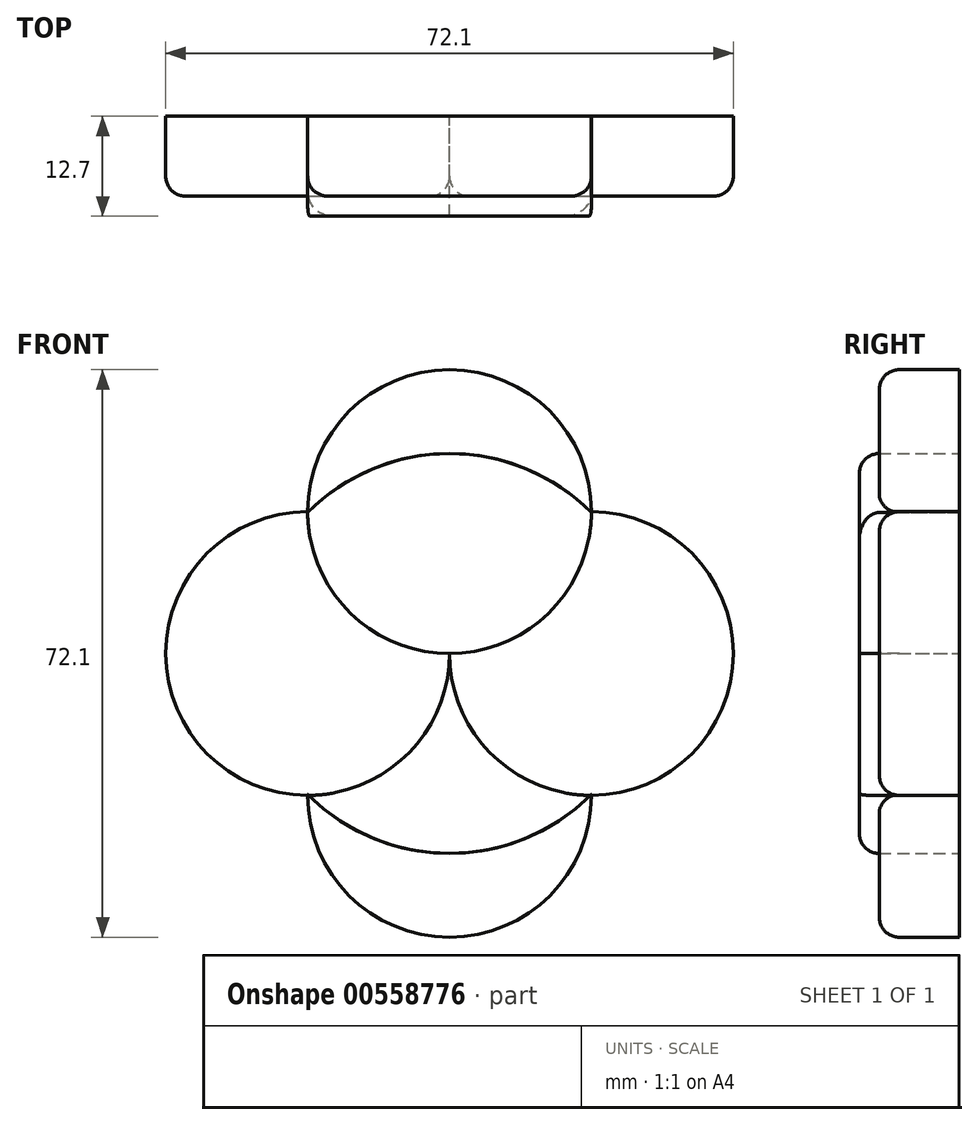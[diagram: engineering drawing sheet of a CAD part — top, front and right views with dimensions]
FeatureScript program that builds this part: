
annotation { "Feature Type Name" : "Feature", "Feature Type Description" : "" }
export const myFeature = defineFeature(function(context is Context, id is Id, definition is map)
    precondition{}
    {
        {
            var Q0;
            Q0=qCreatedBy(makeId("Front.planeOp"),FACE);
            var sketch = newSketch(context, id + "F0", { "sketchPlane" : qUnion([Q0])});
            skCircle(sketch, "E0", {"center": v(0, 18.02) * mm, "radius": 18.02 * mm});
            skCircle(sketch, "E1", {"center": v(18.02, 0) * mm, "radius": 18.02 * mm});
            skCircle(sketch, "E2", {"center": v(0, -18.02) * mm, "radius": 18.02 * mm});
            skCircle(sketch, "E3", {"center": v(-18.02, 0) * mm, "radius": 18.02 * mm});
            skCircle(sketch, "E4", {"center": v(0, 0) * mm, "radius": 25.4 * mm});
            skSolve(sketch);
        }
        {
            var Q0;
            {var subQ0=sQuery(id+"F0.wireOp",EDGE,"E4");var subQ1=sQuery(id+"F0.wireOp",EDGE,"E1");var subQ2=makeQuery(id+"F0.imprint","INTERSECT",VERTEX,{"disambiguationData":[OD(0.0)],"derivedFrom":[subQ1,subQ0]});Q0=makeQuery(id+"F0.imprint","IMPRINT",FACE,{"disambiguationData":[TD([[makeQuery(id+"F0.imprint","IMPRINT",EDGE,{"disambiguationData":[TD([[subQ2,-1.0]])],"derivedFrom":subQ0}),1.0]])]});}
            var Q1;
            {var subQ0=sQuery(id+"F0.wireOp",EDGE,"E4");var subQ1=sQuery(id+"F0.wireOp",EDGE,"E0");var subQ2=makeQuery(id+"F0.imprint","INTERSECT",VERTEX,{"disambiguationData":[OD(0.0)],"derivedFrom":[subQ1,subQ0]});Q1=makeQuery(id+"F0.imprint","IMPRINT",FACE,{"disambiguationData":[TD([[makeQuery(id+"F0.imprint","IMPRINT",EDGE,{"disambiguationData":[TD([[subQ2,-1.0]])],"derivedFrom":subQ0}),1.0]])]});}
            var Q2;
            {var subQ0=sQuery(id+"F0.wireOp",EDGE,"E4");var subQ1=sQuery(id+"F0.wireOp",EDGE,"E0");var subQ2=makeQuery(id+"F0.imprint","INTERSECT",VERTEX,{"disambiguationData":[OD(1.0)],"derivedFrom":[subQ1,subQ0]});Q2=makeQuery(id+"F0.imprint","IMPRINT",FACE,{"disambiguationData":[TD([[makeQuery(id+"F0.imprint","IMPRINT",EDGE,{"disambiguationData":[TD([[subQ2,1.0]])],"derivedFrom":subQ0}),1.0]])]});}
            var Q3;
            {var subQ0=sQuery(id+"F0.wireOp",EDGE,"E4");var subQ1=sQuery(id+"F0.wireOp",EDGE,"E1");var subQ2=makeQuery(id+"F0.imprint","INTERSECT",VERTEX,{"disambiguationData":[OD(1.0)],"derivedFrom":[subQ1,subQ0]});Q3=makeQuery(id+"F0.imprint","IMPRINT",FACE,{"disambiguationData":[TD([[makeQuery(id+"F0.imprint","IMPRINT",EDGE,{"disambiguationData":[TD([[subQ2,1.0]])],"derivedFrom":subQ0}),1.0]])]});}
            extrude(context, id + "F1", {"entities" : qUnion([Q0, Q1, Q2, Q3]), "depth" : 12.7 * mm, "offsetDistance" : 25.4 * mm});
        }
        {
            var Q0;
            {var subQ0=sQuery(id+"F0.wireOp",EDGE,"E4");var subQ1=sQuery(id+"F0.wireOp",EDGE,"E0");var subQ2=makeQuery(id+"F0.imprint","INTERSECT",VERTEX,{"disambiguationData":[OD(0.0)],"derivedFrom":[subQ1,subQ0]});Q0=makeQuery(id+"F0.imprint","IMPRINT",FACE,{"disambiguationData":[TD([[makeQuery(id+"F0.imprint","IMPRINT",EDGE,{"disambiguationData":[TD([[subQ2,1.0]])],"derivedFrom":subQ0}),1.0]])]});}
            var Q1;
            {var subQ0=sQuery(id+"F0.wireOp",EDGE,"E4");var subQ1=sQuery(id+"F0.wireOp",EDGE,"E0");var subQ2=makeQuery(id+"F0.imprint","INTERSECT",VERTEX,{"disambiguationData":[OD(1.0)],"derivedFrom":[subQ1,subQ0]});Q1=makeQuery(id+"F0.imprint","IMPRINT",FACE,{"disambiguationData":[TD([[makeQuery(id+"F0.imprint","IMPRINT",EDGE,{"disambiguationData":[TD([[subQ2,-1.0]])],"derivedFrom":subQ0}),1.0]])]});}
            var Q2;
            {var subQ0=sQuery(id+"F0.wireOp",EDGE,"E4");var subQ1=sQuery(id+"F0.wireOp",EDGE,"E2");var subQ2=makeQuery(id+"F0.imprint","INTERSECT",VERTEX,{"disambiguationData":[OD(1.0)],"derivedFrom":[subQ1,subQ0]});Q2=makeQuery(id+"F0.imprint","IMPRINT",FACE,{"disambiguationData":[TD([[makeQuery(id+"F0.imprint","IMPRINT",EDGE,{"disambiguationData":[TD([[subQ2,-1.0]])],"derivedFrom":subQ0}),1.0]])]});}
            var Q3;
            {var subQ0=sQuery(id+"F0.wireOp",EDGE,"E4");var subQ1=sQuery(id+"F0.wireOp",EDGE,"E1");var subQ2=makeQuery(id+"F0.imprint","INTERSECT",VERTEX,{"disambiguationData":[OD(1.0)],"derivedFrom":[subQ1,subQ0]});Q3=makeQuery(id+"F0.imprint","IMPRINT",FACE,{"disambiguationData":[TD([[makeQuery(id+"F0.imprint","IMPRINT",EDGE,{"disambiguationData":[TD([[subQ2,-1.0]])],"derivedFrom":subQ0}),1.0]])]});}
            var Q4;
            {var subQ0=sQuery(id+"F0.wireOp",EDGE,"E3");var subQ1=sQuery(id+"F0.wireOp",EDGE,"E0");var subQ2=makeQuery(id+"F0.imprint","INTERSECT",VERTEX,{"derivedFrom":[subQ1,subQ0]});Q4=makeQuery(id+"F0.imprint","IMPRINT",FACE,{"disambiguationData":[TD([[makeQuery(id+"F0.imprint","IMPRINT",EDGE,{"disambiguationData":[TD([[subQ2,1.0]])],"derivedFrom":subQ1}),1.0]])]});}
            var Q5;
            {var subQ0=sQuery(id+"F0.wireOp",EDGE,"E1");var subQ1=sQuery(id+"F0.wireOp",EDGE,"E0");var subQ2=makeQuery(id+"F0.imprint","INTERSECT",VERTEX,{"derivedFrom":[subQ1,subQ0]});Q5=makeQuery(id+"F0.imprint","IMPRINT",FACE,{"disambiguationData":[TD([[makeQuery(id+"F0.imprint","IMPRINT",EDGE,{"disambiguationData":[TD([[subQ2,1.0]])],"derivedFrom":subQ1}),-1.0]])]});}
            var Q6;
            {var subQ0=sQuery(id+"F0.wireOp",EDGE,"E3");var subQ1=sQuery(id+"F0.wireOp",EDGE,"E0");var subQ2=makeQuery(id+"F0.imprint","INTERSECT",VERTEX,{"derivedFrom":[subQ1,subQ0]});Q6=makeQuery(id+"F0.imprint","IMPRINT",FACE,{"disambiguationData":[TD([[makeQuery(id+"F0.imprint","IMPRINT",EDGE,{"disambiguationData":[TD([[subQ2,-1.0]])],"derivedFrom":subQ1}),-1.0]])]});}
            var Q7;
            {var subQ0=sQuery(id+"F0.wireOp",EDGE,"E2");var subQ1=sQuery(id+"F0.wireOp",EDGE,"E1");var subQ2=makeQuery(id+"F0.imprint","INTERSECT",VERTEX,{"derivedFrom":[subQ1,subQ0]});Q7=makeQuery(id+"F0.imprint","IMPRINT",FACE,{"disambiguationData":[TD([[makeQuery(id+"F0.imprint","IMPRINT",EDGE,{"disambiguationData":[TD([[subQ2,1.0]])],"derivedFrom":subQ1}),-1.0]])]});}
            extrude(context, id + "F2", {"entities" : qUnion([Q0, Q1, Q2, Q3, Q4, Q5, Q6, Q7]), "depth" : 10.16 * mm, "offsetDistance" : 25.4 * mm});
        }
        {
            var Q0;
            {var subQ0=sQuery(id+"F0.wireOp",EDGE,"E2");Q0=makeQuery(id+"F2.opExtrude","CAP_EDGE",EDGE,{"disambiguationData":[OSD([subQ0]),TDD([makeQuery(id+"F0.imprint","IMPRINT",EDGE,{"disambiguationData":[TD([[makeQuery(id+"F0.imprint","INTERSECT",VERTEX,{"derivedFrom":[sQuery(id+"F0.wireOp",EDGE,"E1"),subQ0]}),1.0]])],"derivedFrom":subQ0})])],"isStart":false});}
            var Q1;
            {var subQ0=sQuery(id+"F0.wireOp",EDGE,"E1");Q1=makeQuery(id+"F2.opExtrude","CAP_EDGE",EDGE,{"disambiguationData":[OSD([subQ0]),TDD([makeQuery(id+"F0.imprint","IMPRINT",EDGE,{"disambiguationData":[TD([[makeQuery(id+"F0.imprint","INTERSECT",VERTEX,{"derivedFrom":[sQuery(id+"F0.wireOp",EDGE,"E0"),subQ0]}),1.0]])],"derivedFrom":subQ0})])],"isStart":false});}
            var Q2;
            {var subQ0=sQuery(id+"F0.wireOp",EDGE,"E0");Q2=makeQuery(id+"F2.opExtrude","CAP_EDGE",EDGE,{"disambiguationData":[OSD([subQ0]),TDD([makeQuery(id+"F0.imprint","IMPRINT",EDGE,{"disambiguationData":[TD([[makeQuery(id+"F0.imprint","INTERSECT",VERTEX,{"derivedFrom":[subQ0,sQuery(id+"F0.wireOp",EDGE,"E3")]}),1.0]])],"derivedFrom":subQ0})])],"isStart":false});}
            var Q3;
            {var subQ0=sQuery(id+"F0.wireOp",EDGE,"E3");Q3=makeQuery(id+"F2.opExtrude","CAP_EDGE",EDGE,{"disambiguationData":[OSD([subQ0]),TDD([makeQuery(id+"F0.imprint","IMPRINT",EDGE,{"disambiguationData":[TD([[makeQuery(id+"F0.imprint","INTERSECT",VERTEX,{"derivedFrom":[sQuery(id+"F0.wireOp",EDGE,"E0"),subQ0]}),-1.0]])],"derivedFrom":subQ0})])],"isStart":false});}
            var Q4;
            {var subQ0=sQuery(id+"F0.wireOp",EDGE,"E4");Q4=makeQuery(id+"F1.opExtrude","CAP_EDGE",EDGE,{"disambiguationData":[OSD([subQ0]),TDD([makeQuery(id+"F0.imprint","IMPRINT",EDGE,{"disambiguationData":[TD([[makeQuery(id+"F0.imprint","INTERSECT",VERTEX,{"disambiguationData":[OD(1.0)],"derivedFrom":[sQuery(id+"F0.wireOp",EDGE,"E0"),subQ0]}),1.0]])],"derivedFrom":subQ0})])],"isStart":false});}
            var Q5;
            {var subQ0=sQuery(id+"F0.wireOp",EDGE,"E4");Q5=makeQuery(id+"F1.opExtrude","CAP_EDGE",EDGE,{"disambiguationData":[OSD([subQ0]),TDD([makeQuery(id+"F0.imprint","IMPRINT",EDGE,{"disambiguationData":[TD([[makeQuery(id+"F0.imprint","INTERSECT",VERTEX,{"disambiguationData":[OD(0.0)],"derivedFrom":[sQuery(id+"F0.wireOp",EDGE,"E1"),subQ0]}),-1.0]])],"derivedFrom":subQ0})])],"isStart":false});}
            var Q6;
            {var subQ0=sQuery(id+"F0.wireOp",EDGE,"E4");Q6=makeQuery(id+"F1.opExtrude","CAP_EDGE",EDGE,{"disambiguationData":[OSD([subQ0]),TDD([makeQuery(id+"F0.imprint","IMPRINT",EDGE,{"disambiguationData":[TD([[makeQuery(id+"F0.imprint","INTERSECT",VERTEX,{"disambiguationData":[OD(0.0)],"derivedFrom":[sQuery(id+"F0.wireOp",EDGE,"E0"),subQ0]}),-1.0]])],"derivedFrom":subQ0})])],"isStart":false});}
            var Q7;
            {var subQ0=sQuery(id+"F0.wireOp",EDGE,"E4");Q7=makeQuery(id+"F1.opExtrude","CAP_EDGE",EDGE,{"disambiguationData":[OSD([subQ0]),TDD([makeQuery(id+"F0.imprint","IMPRINT",EDGE,{"disambiguationData":[TD([[makeQuery(id+"F0.imprint","INTERSECT",VERTEX,{"disambiguationData":[OD(1.0)],"derivedFrom":[sQuery(id+"F0.wireOp",EDGE,"E1"),subQ0]}),1.0]])],"derivedFrom":subQ0})])],"isStart":false});}
            fillet(context, id + "F3", {"entities" : qUnion([Q0, Q1, Q2, Q3, Q4, Q5, Q6, Q7]), "radius" : 2.54 * mm, "tangentPropagation" : true, "allowEdgeOverflow" : false});
        }
    });
